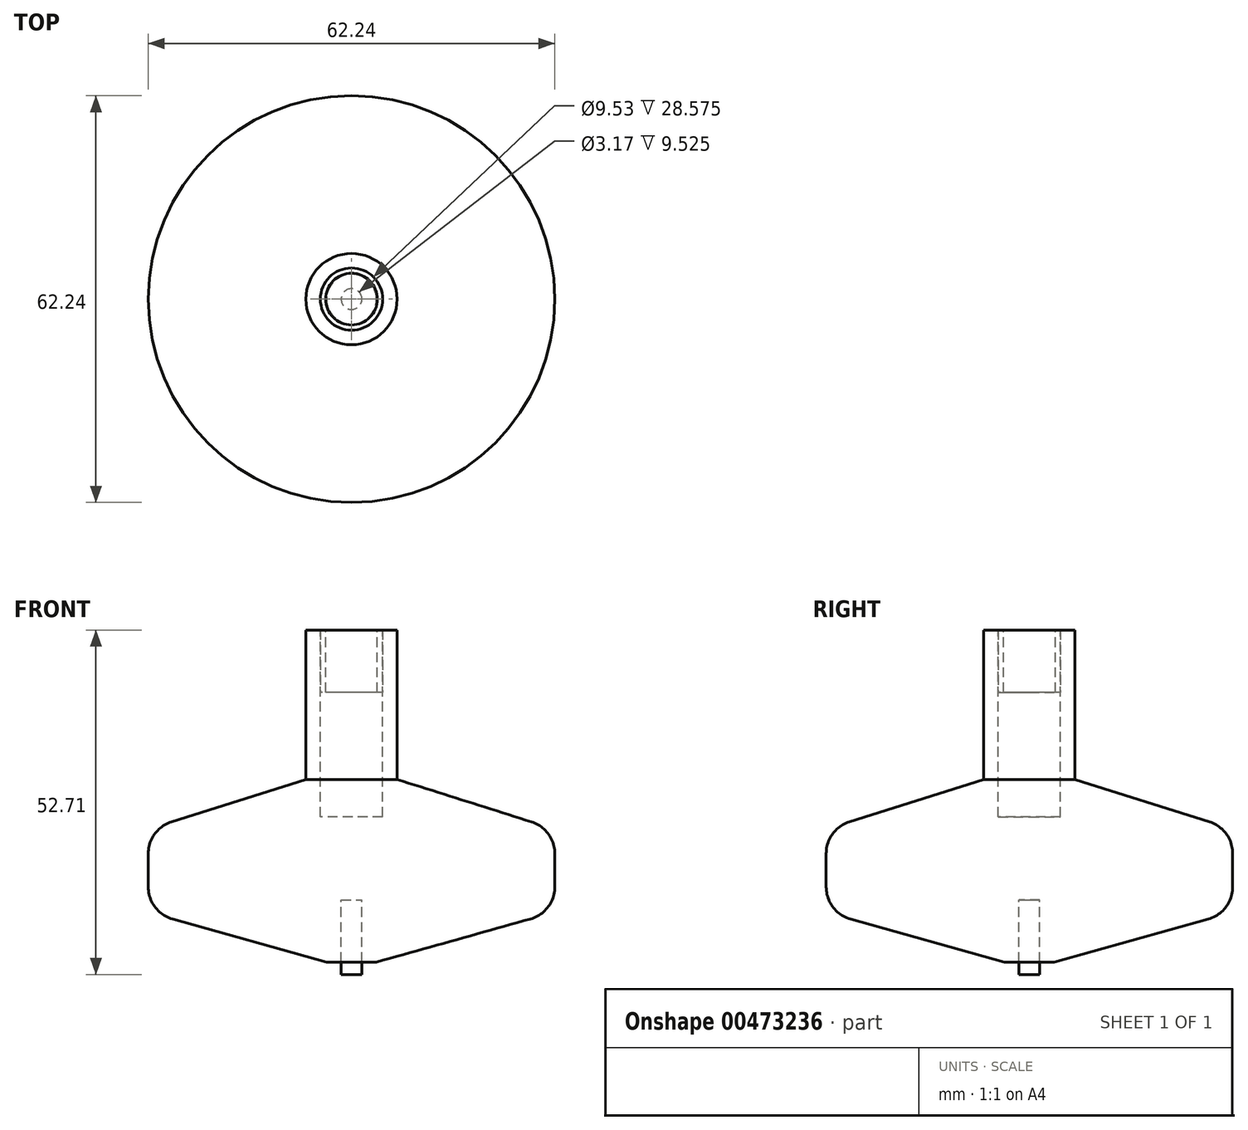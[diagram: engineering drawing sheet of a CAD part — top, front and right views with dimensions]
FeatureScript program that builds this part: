
annotation { "Feature Type Name" : "Feature", "Feature Type Description" : "" }
export const myFeature = defineFeature(function(context is Context, id is Id, definition is map)
    precondition{}
    {
        {
            var Q0;
            Q0=qCreatedBy(makeId("Front.planeOp"),FACE);
            var sketch = newSketch(context, id + "F0", { "sketchPlane" : qUnion([Q0])});
            skLineSegment(sketch, "E0", {"start": v(31.12, 9.53) * mm, "end": v(31.12, 22.23) * mm});
            skLineSegment(sketch, "E1", {"start": v(6.99, 52.7) * mm, "end": v(0, 52.7) * mm});
            skLineSegment(sketch, "E2", {"start": v(0, 52.7) * mm, "end": v(0, 1.9) * mm});
            skLineSegment(sketch, "E3", {"start": v(0, 1.9) * mm, "end": v(3.81, 1.9) * mm});
            skLineSegment(sketch, "E4", {"start": v(3.81, 1.9) * mm, "end": v(31.12, 9.53) * mm});
            skLineSegment(sketch, "E5", {"start": v(31.12, 22.23) * mm, "end": v(6.99, 29.84) * mm});
            skLineSegment(sketch, "E6", {"start": v(6.99, 29.84) * mm, "end": v(6.99, 52.7) * mm});
            skSolve(sketch);
        }
        {
            var Q0;
            Q0=makeQuery(id+"F0.imprint","IMPRINT",FACE,{"disambiguationData":[TD([[makeQuery(id+"F0.imprint","IMPRINT",EDGE,{"derivedFrom":sQuery(id+"F0.wireOp",EDGE,"E0")}),1.0]])]});
            var Q1;
            Q1=sQuery(id+"F0.wireOp",EDGE,"E2");
            revolve(context, id + "F1", {"entities" : qUnion([Q0]), "axis" : qUnion([Q1]), "revolveType" : RevolveType.FULL});
        }
        {
            var Q0;
            Q0=makeQuery(id+"F1.opRevolve","SWEPT_FACE",FACE,{"disambiguationData":[OSD([sQuery(id+"F0.wireOp",EDGE,"E1")])]});
            var sketch = newSketch(context, id + "F2", { "sketchPlane" : qUnion([Q0])});
            skCircle(sketch, "E7", {"center": v(0, 0) * mm, "radius": 4.76 * mm});
            skSolve(sketch);
        }
        {
            var Q0;
            Q0=makeQuery(id+"F2.imprint","IMPRINT",FACE,{"disambiguationData":[TD([[makeQuery(id+"F2.imprint","IMPRINT",EDGE,{"derivedFrom":sQuery(id+"F2.wireOp",EDGE,"E7")}),1.0]])]});
            extrude(context, id + "F3", {"entities" : qUnion([Q0]), "operationType" : NewBodyOperationType.REMOVE, "oppositeDirection" : true, "depth" : 9.52 * mm});
        }
        {
            var Q0;
            Q0=makeQuery(id+"F1.opRevolve","SWEPT_FACE",FACE,{"disambiguationData":[OSD([sQuery(id+"F0.wireOp",EDGE,"E3")])]});
            var sketch = newSketch(context, id + "F4", { "sketchPlane" : qUnion([Q0])});
            skCircle(sketch, "E8", {"center": v(0, 0) * mm, "radius": 1.59 * mm});
            skSolve(sketch);
        }
        {
            var Q0;
            Q0=qSketchRegion(id+"F4",true);
            extrude(context, id + "F5", {"entities" : qUnion([Q0]), "operationType" : NewBodyOperationType.REMOVE, "oppositeDirection" : true, "depth" : 9.52 * mm});
        }
        {
            var Q0;
            Q0=makeQuery(id+"F1.opRevolve","SWEPT_FACE",FACE,{"disambiguationData":[OSD([sQuery(id+"F0.wireOp",EDGE,"E0")])]});
            fillet(context, id + "F6", {"entities" : qUnion([Q0]), "radius" : 5.08 * mm, "tangentPropagation" : true, "allowEdgeOverflow" : false});
        }
        {
            var Q0;
            Q0=makeQuery(id+"F3.boolean.opBoolean","COPY",FACE,{"derivedFrom":makeQuery(id+"F3.opExtrude","CAP_FACE",FACE,{"disambiguationData":[OSD([sQuery(id+"F2.wireOp",EDGE,"E7")])],"isStart":false})});
            extrude(context, id + "F7", {"entities" : qUnion([Q0]), "depth" : 9.52 * mm});
        }
        {
            var Q0;
            Q0=makeQuery(id+"F7.opExtrude","CAP_FACE",FACE,{"disambiguationData":[OSD([sQuery(id+"F2.wireOp",EDGE,"E7")])],"isStart":false});
            var sketch = newSketch(context, id + "F8", { "sketchPlane" : qUnion([Q0])});
            skCircle(sketch, "E9", {"center": v(0, 0) * mm, "radius": 3.95 * mm});
            skSolve(sketch);
        }
        {
            var Q0;
            Q0=makeQuery(id+"F8.imprint","IMPRINT",FACE,{"disambiguationData":[TD([[makeQuery(id+"F8.imprint","IMPRINT",EDGE,{"derivedFrom":sQuery(id+"F8.wireOp",EDGE,"E9")}),1.0]])]});
            extrude(context, id + "F9", {"entities" : qUnion([Q0]), "operationType" : NewBodyOperationType.REMOVE, "oppositeDirection" : true, "depth" : 9.52 * mm});
        }
        {
            var Q0;
            Q0=makeQuery(id+"F5.boolean.opBoolean","COPY",FACE,{"derivedFrom":makeQuery(id+"F5.opExtrude","CAP_FACE",FACE,{"disambiguationData":[OSD([sQuery(id+"F4.wireOp",EDGE,"E8")])],"isStart":false})});
            extrude(context, id + "F10", {"entities" : qUnion([Q0]), "depth" : 11.43 * mm});
        }
        {
            var Q0;
            Q0=makeQuery(id+"F3.boolean.opBoolean","COPY",FACE,{"derivedFrom":makeQuery(id+"F3.opExtrude","CAP_FACE",FACE,{"disambiguationData":[OSD([sQuery(id+"F2.wireOp",EDGE,"E7")])],"isStart":false})});
            extrude(context, id + "F11", {"entities" : qUnion([Q0]), "operationType" : NewBodyOperationType.REMOVE, "oppositeDirection" : true, "depth" : 19.05 * mm});
        }
    });
